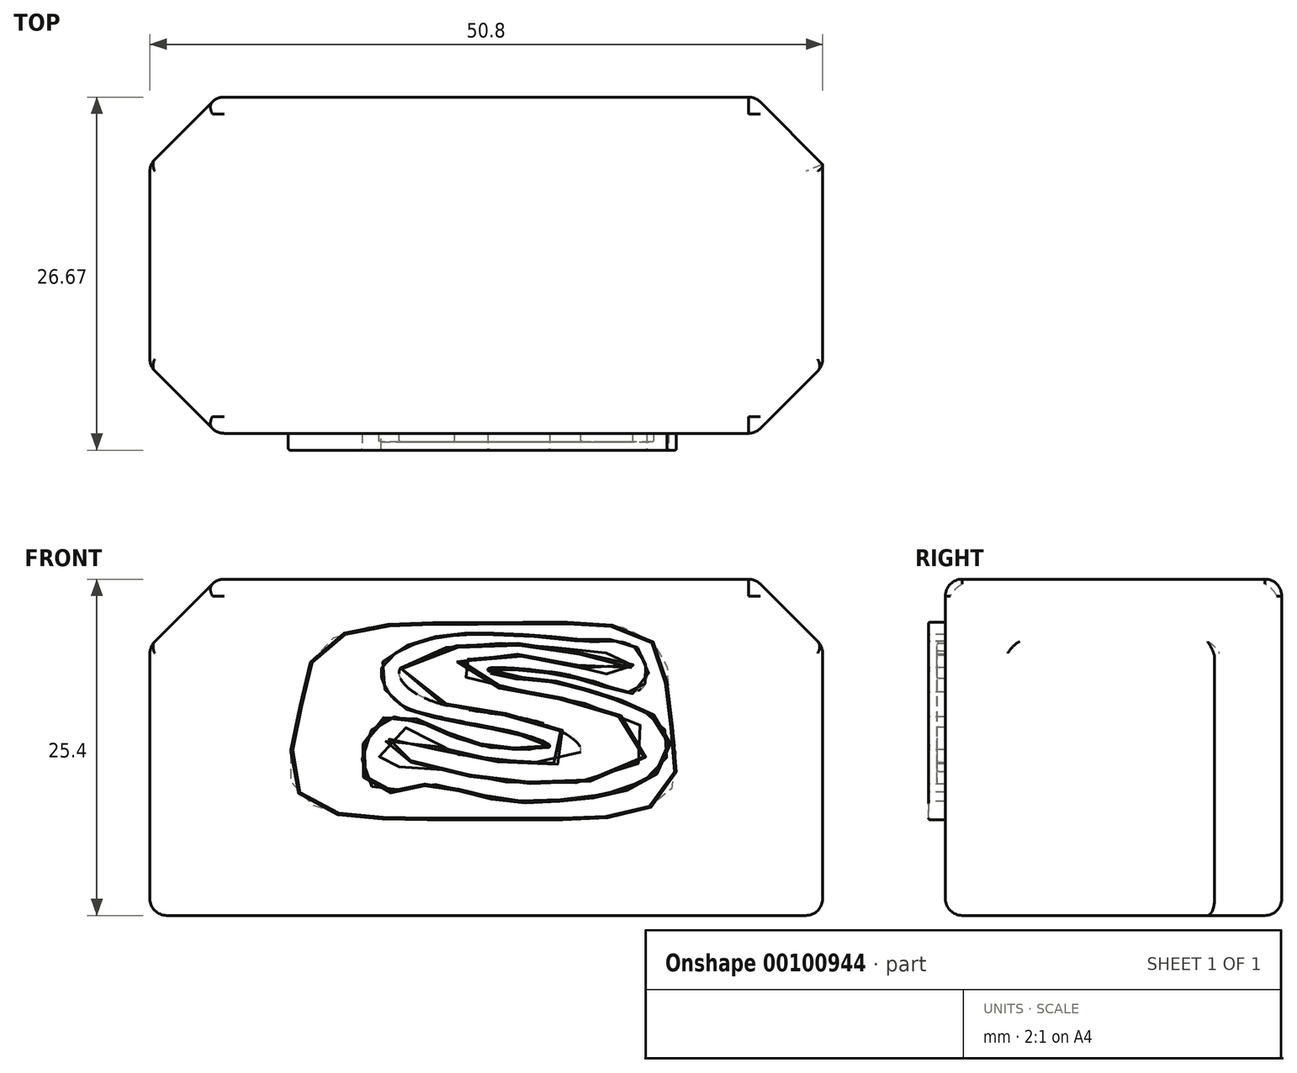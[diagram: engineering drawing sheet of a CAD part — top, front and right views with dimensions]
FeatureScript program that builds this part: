
annotation { "Feature Type Name" : "Feature", "Feature Type Description" : "" }
export const myFeature = defineFeature(function(context is Context, id is Id, definition is map)
    precondition{}
    {
        {
            var Q0;
            Q0=qCreatedBy(makeId("Top.planeOp"),FACE);
            var sketch = newSketch(context, id + "F0", { "sketchPlane" : qUnion([Q0])});
            skLineSegment(sketch, "E0.bottom", {"start": v(0, 0) * mm, "end": v(50.8, 0) * mm});
            skLineSegment(sketch, "E0.top", {"start": v(0, -25.4) * mm, "end": v(50.8, -25.4) * mm});
            skLineSegment(sketch, "E0.left", {"start": v(0, 0) * mm, "end": v(0, -25.4) * mm});
            skLineSegment(sketch, "E0.right", {"start": v(50.8, 0) * mm, "end": v(50.8, -25.4) * mm});
            skSolve(sketch);
        }
        {
            var Q0;
            Q0=makeQuery(id+"F0.imprint","IMPRINT",FACE,{"disambiguationData":[TD([[makeQuery(id+"F0.imprint","IMPRINT",EDGE,{"derivedFrom":sQuery(id+"F0.wireOp",EDGE,"E0.bottom")}),-1.0]])]});
            extrude(context, id + "F1", {"entities" : qUnion([Q0]), "depth" : 25.4 * mm});
        }
        {
            var Q0;
            Q0=makeQuery(id+"F1.opExtrude","CAP_EDGE",EDGE,{"disambiguationData":[OSD([sQuery(id+"F0.wireOp",EDGE,"E0.left")])],"isStart":false});
            var Q1;
            Q1=makeQuery(id+"F1.opExtrude","CAP_EDGE",EDGE,{"disambiguationData":[OSD([sQuery(id+"F0.wireOp",EDGE,"E0.right")])],"isStart":false});
            var Q2;
            Q2=makeQuery(id+"F1.opExtrude","SWEPT_EDGE",EDGE,{"disambiguationData":[OSD([sQuery(id+"F0.wireOp",EDGE,"E0.top"),sQuery(id+"F0.wireOp",EDGE,"E0.left")])]});
            var Q3;
            Q3=makeQuery(id+"F1.opExtrude","SWEPT_EDGE",EDGE,{"disambiguationData":[OSD([sQuery(id+"F0.wireOp",EDGE,"E0.top"),sQuery(id+"F0.wireOp",EDGE,"E0.right")])]});
            var Q4;
            Q4=makeQuery(id+"F1.opExtrude","SWEPT_EDGE",EDGE,{"disambiguationData":[OSD([sQuery(id+"F0.wireOp",EDGE,"E0.bottom"),sQuery(id+"F0.wireOp",EDGE,"E0.right")])]});
            var Q5;
            Q5=makeQuery(id+"F1.opExtrude","SWEPT_EDGE",EDGE,{"disambiguationData":[OSD([sQuery(id+"F0.wireOp",EDGE,"E0.bottom"),sQuery(id+"F0.wireOp",EDGE,"E0.left")])]});
            chamfer(context, id + "F2", {"entities" : qUnion([Q0, Q1, Q2, Q3, Q4, Q5]), "width" : 5.08 * mm, "tangentPropagation" : true});
        }
        {
            var Q0;
            Q0=makeQuery(id+"F1.opExtrude","CAP_EDGE",EDGE,{"disambiguationData":[OSD([sQuery(id+"F0.wireOp",EDGE,"E0.top")])],"isStart":false});
            var Q1;
            Q1=makeQuery(id+"F1.opExtrude","CAP_EDGE",EDGE,{"disambiguationData":[OSD([sQuery(id+"F0.wireOp",EDGE,"E0.bottom")])],"isStart":false});
            var Q2;
            {var subQ0=sQuery(id+"F0.wireOp",EDGE,"E0.right");var subQ1=sQuery(id+"F0.wireOp",EDGE,"E0.left");var subQ2=sQuery(id+"F0.wireOp",EDGE,"E0.top");var subQ3=sQuery(id+"F0.wireOp",EDGE,"E0.bottom");Q2=makeQuery(id+"F2.opChamfer","BLEND_EDGE",EDGE,{"blendedFrom":[makeQuery(id+"F1.opExtrude","CAP_EDGE",EDGE,{"disambiguationData":[OSD([subQ0])],"isStart":false}),makeQuery(id+"FMAaeaN72eKezCo_1.boolean.opBoolean","SPLIT",FACE,{"disambiguationData":[TD([makeQuery(id+"F1.opExtrude","SWEPT_FACE",FACE,{"disambiguationData":[OSD([subQ3])]})])],"derivedFrom":makeQuery(id+"F1.opExtrude","CAP_FACE",FACE,{"disambiguationData":[OSD([subQ3,subQ2,subQ1,subQ0])],"isStart":false})})],"blendedInto":[makeQuery(id+"FMAaeaN72eKezCo_1.boolean.opBoolean","SPLIT",FACE,{"disambiguationData":[TD([makeQuery(id+"F1.opExtrude","SWEPT_FACE",FACE,{"disambiguationData":[OSD([subQ3])]})])],"derivedFrom":makeQuery(id+"F1.opExtrude","CAP_FACE",FACE,{"disambiguationData":[OSD([subQ3,subQ2,subQ1,subQ0])],"isStart":false})})]});}
            var Q3;
            {var subQ0=sQuery(id+"F0.wireOp",EDGE,"E0.right");Q3=makeQuery(id+"F2.opChamfer","BLEND_EDGE",EDGE,{"blendedFrom":[makeQuery(id+"F1.opExtrude","SWEPT_EDGE",EDGE,{"disambiguationData":[OSD([sQuery(id+"F0.wireOp",EDGE,"E0.bottom"),subQ0])]}),makeQuery(id+"F1.opExtrude","CAP_EDGE",EDGE,{"disambiguationData":[OSD([subQ0])],"isStart":false})],"blendedInto":[]});}
            var Q4;
            {var subQ0=sQuery(id+"F0.wireOp",EDGE,"E0.right");Q4=makeQuery(id+"F2.opChamfer","BLEND_EDGE",EDGE,{"blendedFrom":[makeQuery(id+"F1.opExtrude","SWEPT_EDGE",EDGE,{"disambiguationData":[OSD([sQuery(id+"F0.wireOp",EDGE,"E0.top"),subQ0])]}),makeQuery(id+"F1.opExtrude","CAP_EDGE",EDGE,{"disambiguationData":[OSD([subQ0])],"isStart":false})],"blendedInto":[]});}
            var Q5;
            {var subQ0=sQuery(id+"F0.wireOp",EDGE,"E0.top");Q5=makeQuery(id+"F2.opChamfer","BLEND_EDGE",EDGE,{"blendedFrom":[makeQuery(id+"F1.opExtrude","SWEPT_EDGE",EDGE,{"disambiguationData":[OSD([subQ0,sQuery(id+"F0.wireOp",EDGE,"E0.right")])]}),makeQuery(id+"F1.opExtrude","SWEPT_FACE",FACE,{"disambiguationData":[OSD([subQ0])]})],"blendedInto":[makeQuery(id+"F1.opExtrude","SWEPT_FACE",FACE,{"disambiguationData":[OSD([subQ0])]})]});}
            var Q6;
            Q6=makeQuery(id+"F1.opExtrude","CAP_EDGE",EDGE,{"disambiguationData":[OSD([sQuery(id+"F0.wireOp",EDGE,"E0.right")])],"isStart":true});
            var Q7;
            {var subQ0=sQuery(id+"F0.wireOp",EDGE,"E0.top");Q7=makeQuery(id+"F2.opChamfer","BLEND_EDGE",EDGE,{"blendedFrom":[makeQuery(id+"F1.opExtrude","SWEPT_EDGE",EDGE,{"disambiguationData":[OSD([subQ0,sQuery(id+"F0.wireOp",EDGE,"E0.left")])]}),makeQuery(id+"F1.opExtrude","SWEPT_FACE",FACE,{"disambiguationData":[OSD([subQ0])]})],"blendedInto":[makeQuery(id+"F1.opExtrude","SWEPT_FACE",FACE,{"disambiguationData":[OSD([subQ0])]})]});}
            var Q8;
            {var subQ0=sQuery(id+"F0.wireOp",EDGE,"E0.left");Q8=makeQuery(id+"F2.opChamfer","BLEND_EDGE",EDGE,{"blendedFrom":[makeQuery(id+"F1.opExtrude","SWEPT_EDGE",EDGE,{"disambiguationData":[OSD([sQuery(id+"F0.wireOp",EDGE,"E0.top"),subQ0])]}),makeQuery(id+"F1.opExtrude","SWEPT_FACE",FACE,{"disambiguationData":[OSD([subQ0])]})],"blendedInto":[makeQuery(id+"F1.opExtrude","SWEPT_FACE",FACE,{"disambiguationData":[OSD([subQ0])]})]});}
            var Q9;
            {var subQ0=sQuery(id+"F0.wireOp",EDGE,"E0.left");Q9=makeQuery(id+"F2.opChamfer","BLEND_EDGE",EDGE,{"blendedFrom":[makeQuery(id+"F1.opExtrude","SWEPT_EDGE",EDGE,{"disambiguationData":[OSD([sQuery(id+"F0.wireOp",EDGE,"E0.top"),subQ0])]}),makeQuery(id+"F1.opExtrude","CAP_EDGE",EDGE,{"disambiguationData":[OSD([subQ0])],"isStart":false})],"blendedInto":[]});}
            var Q10;
            {var subQ0=sQuery(id+"F0.wireOp",EDGE,"E0.right");var subQ1=sQuery(id+"F0.wireOp",EDGE,"E0.left");var subQ2=sQuery(id+"F0.wireOp",EDGE,"E0.top");var subQ3=sQuery(id+"F0.wireOp",EDGE,"E0.bottom");Q10=makeQuery(id+"F2.opChamfer","BLEND_EDGE",EDGE,{"blendedFrom":[makeQuery(id+"F1.opExtrude","CAP_EDGE",EDGE,{"disambiguationData":[OSD([subQ1])],"isStart":false}),makeQuery(id+"FMAaeaN72eKezCo_1.boolean.opBoolean","SPLIT",FACE,{"disambiguationData":[TD([makeQuery(id+"F1.opExtrude","SWEPT_FACE",FACE,{"disambiguationData":[OSD([subQ3])]})])],"derivedFrom":makeQuery(id+"F1.opExtrude","CAP_FACE",FACE,{"disambiguationData":[OSD([subQ3,subQ2,subQ1,subQ0])],"isStart":false})})],"blendedInto":[makeQuery(id+"FMAaeaN72eKezCo_1.boolean.opBoolean","SPLIT",FACE,{"disambiguationData":[TD([makeQuery(id+"F1.opExtrude","SWEPT_FACE",FACE,{"disambiguationData":[OSD([subQ3])]})])],"derivedFrom":makeQuery(id+"F1.opExtrude","CAP_FACE",FACE,{"disambiguationData":[OSD([subQ3,subQ2,subQ1,subQ0])],"isStart":false})})]});}
            var Q11;
            {var subQ0=sQuery(id+"F0.wireOp",EDGE,"E0.left");Q11=makeQuery(id+"F2.opChamfer","BLEND_EDGE",EDGE,{"blendedFrom":[makeQuery(id+"F1.opExtrude","CAP_EDGE",EDGE,{"disambiguationData":[OSD([subQ0])],"isStart":false}),makeQuery(id+"F1.opExtrude","SWEPT_FACE",FACE,{"disambiguationData":[OSD([subQ0])]})],"blendedInto":[makeQuery(id+"F1.opExtrude","SWEPT_FACE",FACE,{"disambiguationData":[OSD([subQ0])]})]});}
            var Q12;
            {var subQ0=sQuery(id+"F0.wireOp",EDGE,"E0.left");Q12=makeQuery(id+"F2.opChamfer","BLEND_EDGE",EDGE,{"blendedFrom":[makeQuery(id+"F1.opExtrude","SWEPT_EDGE",EDGE,{"disambiguationData":[OSD([sQuery(id+"F0.wireOp",EDGE,"E0.bottom"),subQ0])]}),makeQuery(id+"F1.opExtrude","CAP_EDGE",EDGE,{"disambiguationData":[OSD([subQ0])],"isStart":false})],"blendedInto":[]});}
            var Q13;
            {var subQ0=sQuery(id+"F0.wireOp",EDGE,"E0.left");Q13=makeQuery(id+"F2.opChamfer","BLEND_EDGE",EDGE,{"blendedFrom":[makeQuery(id+"F1.opExtrude","SWEPT_EDGE",EDGE,{"disambiguationData":[OSD([sQuery(id+"F0.wireOp",EDGE,"E0.bottom"),subQ0])]}),makeQuery(id+"F1.opExtrude","SWEPT_FACE",FACE,{"disambiguationData":[OSD([subQ0])]})],"blendedInto":[makeQuery(id+"F1.opExtrude","SWEPT_FACE",FACE,{"disambiguationData":[OSD([subQ0])]})]});}
            var Q14;
            {var subQ0=sQuery(id+"F0.wireOp",EDGE,"E0.bottom");Q14=makeQuery(id+"F2.opChamfer","BLEND_EDGE",EDGE,{"blendedFrom":[makeQuery(id+"F1.opExtrude","SWEPT_EDGE",EDGE,{"disambiguationData":[OSD([subQ0,sQuery(id+"F0.wireOp",EDGE,"E0.left")])]}),makeQuery(id+"F1.opExtrude","SWEPT_FACE",FACE,{"disambiguationData":[OSD([subQ0])]})],"blendedInto":[makeQuery(id+"F1.opExtrude","SWEPT_FACE",FACE,{"disambiguationData":[OSD([subQ0])]})]});}
            var Q15;
            {var subQ0=sQuery(id+"F0.wireOp",EDGE,"E0.bottom");Q15=makeQuery(id+"F2.opChamfer","BLEND_EDGE",EDGE,{"blendedFrom":[makeQuery(id+"F1.opExtrude","SWEPT_EDGE",EDGE,{"disambiguationData":[OSD([subQ0,sQuery(id+"F0.wireOp",EDGE,"E0.right")])]}),makeQuery(id+"F1.opExtrude","SWEPT_FACE",FACE,{"disambiguationData":[OSD([subQ0])]})],"blendedInto":[makeQuery(id+"F1.opExtrude","SWEPT_FACE",FACE,{"disambiguationData":[OSD([subQ0])]})]});}
            var Q16;
            {var subQ0=sQuery(id+"F0.wireOp",EDGE,"E0.right");Q16=makeQuery(id+"F2.opChamfer","BLEND_EDGE",EDGE,{"blendedFrom":[makeQuery(id+"F1.opExtrude","SWEPT_EDGE",EDGE,{"disambiguationData":[OSD([sQuery(id+"F0.wireOp",EDGE,"E0.top"),subQ0])]}),makeQuery(id+"F1.opExtrude","SWEPT_FACE",FACE,{"disambiguationData":[OSD([subQ0])]})],"blendedInto":[makeQuery(id+"F1.opExtrude","SWEPT_FACE",FACE,{"disambiguationData":[OSD([subQ0])]})]});}
            var Q17;
            {var subQ0=sQuery(id+"F0.wireOp",EDGE,"E0.right");Q17=makeQuery(id+"F2.opChamfer","BLEND_EDGE",EDGE,{"blendedFrom":[makeQuery(id+"F1.opExtrude","CAP_EDGE",EDGE,{"disambiguationData":[OSD([subQ0])],"isStart":false}),makeQuery(id+"F1.opExtrude","SWEPT_FACE",FACE,{"disambiguationData":[OSD([subQ0])]})],"blendedInto":[makeQuery(id+"F1.opExtrude","SWEPT_FACE",FACE,{"disambiguationData":[OSD([subQ0])]})]});}
            var Q18;
            {var subQ0=sQuery(id+"F0.wireOp",EDGE,"E0.left");var subQ1=sQuery(id+"F0.wireOp",EDGE,"E0.bottom");Q18=makeQuery(id+"F2.opChamfer","BLEND_EDGE",EDGE,{"blendedFrom":[makeQuery(id+"F1.opExtrude","SWEPT_EDGE",EDGE,{"disambiguationData":[OSD([subQ1,subQ0])]}),makeQuery(id+"F1.opExtrude","CAP_FACE",FACE,{"disambiguationData":[OSD([subQ1,sQuery(id+"F0.wireOp",EDGE,"E0.top"),subQ0,sQuery(id+"F0.wireOp",EDGE,"E0.right")])],"isStart":true})],"blendedInto":[makeQuery(id+"F1.opExtrude","CAP_FACE",FACE,{"disambiguationData":[OSD([subQ1,sQuery(id+"F0.wireOp",EDGE,"E0.top"),subQ0,sQuery(id+"F0.wireOp",EDGE,"E0.right")])],"isStart":true})]});}
            var Q19;
            Q19=makeQuery(id+"F1.opExtrude","CAP_EDGE",EDGE,{"disambiguationData":[OSD([sQuery(id+"F0.wireOp",EDGE,"E0.left")])],"isStart":true});
            var Q20;
            Q20=makeQuery(id+"F1.opExtrude","CAP_EDGE",EDGE,{"disambiguationData":[OSD([sQuery(id+"F0.wireOp",EDGE,"E0.bottom")])],"isStart":true});
            var Q21;
            {var subQ0=sQuery(id+"F0.wireOp",EDGE,"E0.right");var subQ1=sQuery(id+"F0.wireOp",EDGE,"E0.bottom");Q21=makeQuery(id+"F2.opChamfer","BLEND_EDGE",EDGE,{"blendedFrom":[makeQuery(id+"F1.opExtrude","SWEPT_EDGE",EDGE,{"disambiguationData":[OSD([subQ1,subQ0])]}),makeQuery(id+"F1.opExtrude","CAP_FACE",FACE,{"disambiguationData":[OSD([subQ1,sQuery(id+"F0.wireOp",EDGE,"E0.top"),sQuery(id+"F0.wireOp",EDGE,"E0.left"),subQ0])],"isStart":true})],"blendedInto":[makeQuery(id+"F1.opExtrude","CAP_FACE",FACE,{"disambiguationData":[OSD([subQ1,sQuery(id+"F0.wireOp",EDGE,"E0.top"),sQuery(id+"F0.wireOp",EDGE,"E0.left"),subQ0])],"isStart":true})]});}
            var Q22;
            {var subQ0=sQuery(id+"F0.wireOp",EDGE,"E0.right");var subQ1=sQuery(id+"F0.wireOp",EDGE,"E0.top");Q22=makeQuery(id+"F2.opChamfer","BLEND_EDGE",EDGE,{"blendedFrom":[makeQuery(id+"F1.opExtrude","SWEPT_EDGE",EDGE,{"disambiguationData":[OSD([subQ1,subQ0])]}),makeQuery(id+"F1.opExtrude","CAP_FACE",FACE,{"disambiguationData":[OSD([sQuery(id+"F0.wireOp",EDGE,"E0.bottom"),subQ1,sQuery(id+"F0.wireOp",EDGE,"E0.left"),subQ0])],"isStart":true})],"blendedInto":[makeQuery(id+"F1.opExtrude","CAP_FACE",FACE,{"disambiguationData":[OSD([sQuery(id+"F0.wireOp",EDGE,"E0.bottom"),subQ1,sQuery(id+"F0.wireOp",EDGE,"E0.left"),subQ0])],"isStart":true})]});}
            var Q23;
            Q23=makeQuery(id+"F1.opExtrude","CAP_EDGE",EDGE,{"disambiguationData":[OSD([sQuery(id+"F0.wireOp",EDGE,"E0.top")])],"isStart":true});
            var Q24;
            {var subQ0=sQuery(id+"F0.wireOp",EDGE,"E0.left");var subQ1=sQuery(id+"F0.wireOp",EDGE,"E0.top");Q24=makeQuery(id+"F2.opChamfer","BLEND_EDGE",EDGE,{"blendedFrom":[makeQuery(id+"F1.opExtrude","SWEPT_EDGE",EDGE,{"disambiguationData":[OSD([subQ1,subQ0])]}),makeQuery(id+"F1.opExtrude","CAP_FACE",FACE,{"disambiguationData":[OSD([sQuery(id+"F0.wireOp",EDGE,"E0.bottom"),subQ1,subQ0,sQuery(id+"F0.wireOp",EDGE,"E0.right")])],"isStart":true})],"blendedInto":[makeQuery(id+"F1.opExtrude","CAP_FACE",FACE,{"disambiguationData":[OSD([sQuery(id+"F0.wireOp",EDGE,"E0.bottom"),subQ1,subQ0,sQuery(id+"F0.wireOp",EDGE,"E0.right")])],"isStart":true})]});}
            fillet(context, id + "F3", {"entities" : qUnion([Q0, Q1, Q2, Q3, Q4, Q5, Q6, Q7, Q8, Q9, Q10, Q11, Q12, Q13, Q14, Q15, Q16, Q17, Q18, Q19, Q20, Q21, Q22, Q23, Q24]), "radius" : 1.27 * mm, "tangentPropagation" : true, "allowEdgeOverflow" : false});
        }
        {
            var Q0;
            Q0=makeQuery(id+"F1.opExtrude","SWEPT_FACE",FACE,{"disambiguationData":[OSD([sQuery(id+"F0.wireOp",EDGE,"E0.top")])]});
            var sketch = newSketch(context, id + "F4", { "sketchPlane" : qUnion([Q0])});
            skFitSpline(sketch, "E1", {"points": [v(12.12, 19.14) * mm, v(14.19, 21.12) * mm, v(18.19, 22) * mm, v(25.87, 22.13) * mm, v(33.54, 22.09) * mm, v(36.76, 21.4) * mm, v(38.83, 19.74) * mm, v(39.06, 17.26) * mm, v(39.75, 11.74) * mm, v(38.97, 8.98) * mm, v(35.57, 7.51) * mm, v(26.7, 7.23) * mm, v(15.47, 7.42) * mm, v(12.07, 8.48) * mm, v(10.5, 10.55) * mm, v(11.01, 14.04) * mm, v(12.12, 19.14) * mm]});
            skFitSpline(sketch, "E2", {"points": [v(17.5, 18.68) * mm, v(19.61, 20.34) * mm, v(23.18, 21.17) * mm, v(26.93, 21.17) * mm, v(30.06, 20.97) * mm, v(33.15, 20.68) * mm, v(35.24, 20.7) * mm, v(37.03, 19.83) * mm, v(37.42, 17.57) * mm, v(36.38, 16.88) * mm, v(33.9, 17.55) * mm, v(30.31, 18.4) * mm, v(26.45, 18.72) * mm, v(25.52, 18.6) * mm, v(25.9, 18.17) * mm, v(28.15, 17.85) * mm, v(30.81, 17.56) * mm, v(34.03, 16.65) * mm, v(37.4, 15.37) * mm, v(38.93, 13.94) * mm, v(38.9, 11.69) * mm, v(36.13, 9.62) * mm, v(30.56, 8.71) * mm, v(25.94, 8.89) * mm, v(20.46, 9.92) * mm, v(17.43, 9.37) * mm, v(16.1, 10.94) * mm, v(16.48, 13.6) * mm, v(18.14, 14.98) * mm, v(21.1, 14.32) * mm, v(24.07, 13.06) * mm, v(27.96, 12.53) * mm, v(30.2, 12.77) * mm, v(28.86, 13.48) * mm, v(24.76, 14.42) * mm, v(20.98, 15.2) * mm, v(18.86, 15.98) * mm, v(17.92, 17.03) * mm, v(17.5, 18.68) * mm]});
            skFitSpline(sketch, "E3", {"points": [v(18.9, 18.68) * mm, v(21.27, 20) * mm, v(24.35, 20.47) * mm, v(27.84, 20.55) * mm, v(30.88, 20.16) * mm, v(34.02, 19.77) * mm, v(35.56, 19.98) * mm, v(36.46, 19.14) * mm, v(36.07, 18.02) * mm, v(34.92, 18.1) * mm, v(32.66, 18.68) * mm, v(30.71, 19.14) * mm, v(28.08, 19.6) * mm, v(25.5, 19.62) * mm, v(23.42, 19.14) * mm, v(23.01, 18.68) * mm, v(24.13, 17.87) * mm, v(26.8, 17.22) * mm, v(31.97, 16.25) * mm, v(35.77, 15) * mm, v(38.04, 13.2) * mm, v(36, 10.96) * mm, v(31.2, 9.97) * mm, v(25.86, 10.19) * mm, v(21.71, 11.13) * mm, v(19.29, 11.51) * mm, v(18.23, 10.88) * mm, v(17.38, 11.36) * mm, v(17.5, 12.53) * mm, v(18.92, 14.24) * mm, v(21.28, 12.88) * mm, v(26.75, 11.7) * mm, v(31.46, 11.66) * mm, v(32.55, 12.53) * mm, v(30.7, 14.09) * mm, v(27.26, 15.06) * mm, v(22.14, 15.93) * mm, v(19.28, 17.4) * mm, v(18.9, 18.68) * mm]});
            skSolve(sketch);
        }
        {
            var Q0;
            Q0=qSketchRegion(id+"F4",true);
            extrude(context, id + "F5", {"entities" : qUnion([Q0]), "operationType" : NewBodyOperationType.ADD, "depth" : 1.27 * mm});
        }
        {
            var Q0;
            Q0=makeQuery(id+"F5.opExtrude","CAP_EDGE",EDGE,{"disambiguationData":[OSD([sQuery(id+"F4.wireOp",EDGE,"E1")])],"isStart":false});
            var Q1;
            Q1=makeQuery(id+"F5.opExtrude","CAP_EDGE",EDGE,{"disambiguationData":[OSD([sQuery(id+"F4.wireOp",EDGE,"E2")])],"isStart":false});
            var Q2;
            Q2=makeQuery(id+"F5.opExtrude","CAP_EDGE",EDGE,{"disambiguationData":[OSD([sQuery(id+"F4.wireOp",EDGE,"E2")])],"isStart":true});
            var Q3;
            Q3=makeQuery(id+"F5.opExtrude","CAP_EDGE",EDGE,{"disambiguationData":[OSD([sQuery(id+"F4.wireOp",EDGE,"E1")])],"isStart":true});
            fillet(context, id + "F6", {"entities" : qUnion([Q0, Q1, Q2, Q3]), "radius" : 0.13 * mm, "tangentPropagation" : true, "allowEdgeOverflow" : false});
        }
        {
            var Q0;
            Q0=makeQuery(id+"F4.imprint","IMPRINT",FACE,{"disambiguationData":[TD([[makeQuery(id+"F4.imprint","IMPRINT",EDGE,{"derivedFrom":sQuery(id+"F4.wireOp",EDGE,"E3")}),-1.0]])]});
            extrude(context, id + "F7", {"entities" : qUnion([Q0]), "operationType" : NewBodyOperationType.ADD, "depth" : 0.64 * mm});
        }
        {
            var Q0;
            Q0=makeQuery(id+"F7.opExtrude","CAP_FACE",FACE,{"disambiguationData":[OSD([sQuery(id+"F4.wireOp",EDGE,"E3")])],"isStart":false});
            var Q1;
            Q1=makeQuery(id+"F7.opExtrude","CAP_EDGE",EDGE,{"disambiguationData":[OSD([sQuery(id+"F4.wireOp",EDGE,"E3")])],"isStart":true});
            fillet(context, id + "F8", {"entities" : qUnion([Q0, Q1]), "radius" : 0.13 * mm, "tangentPropagation" : true, "allowEdgeOverflow" : false});
        }
    });
